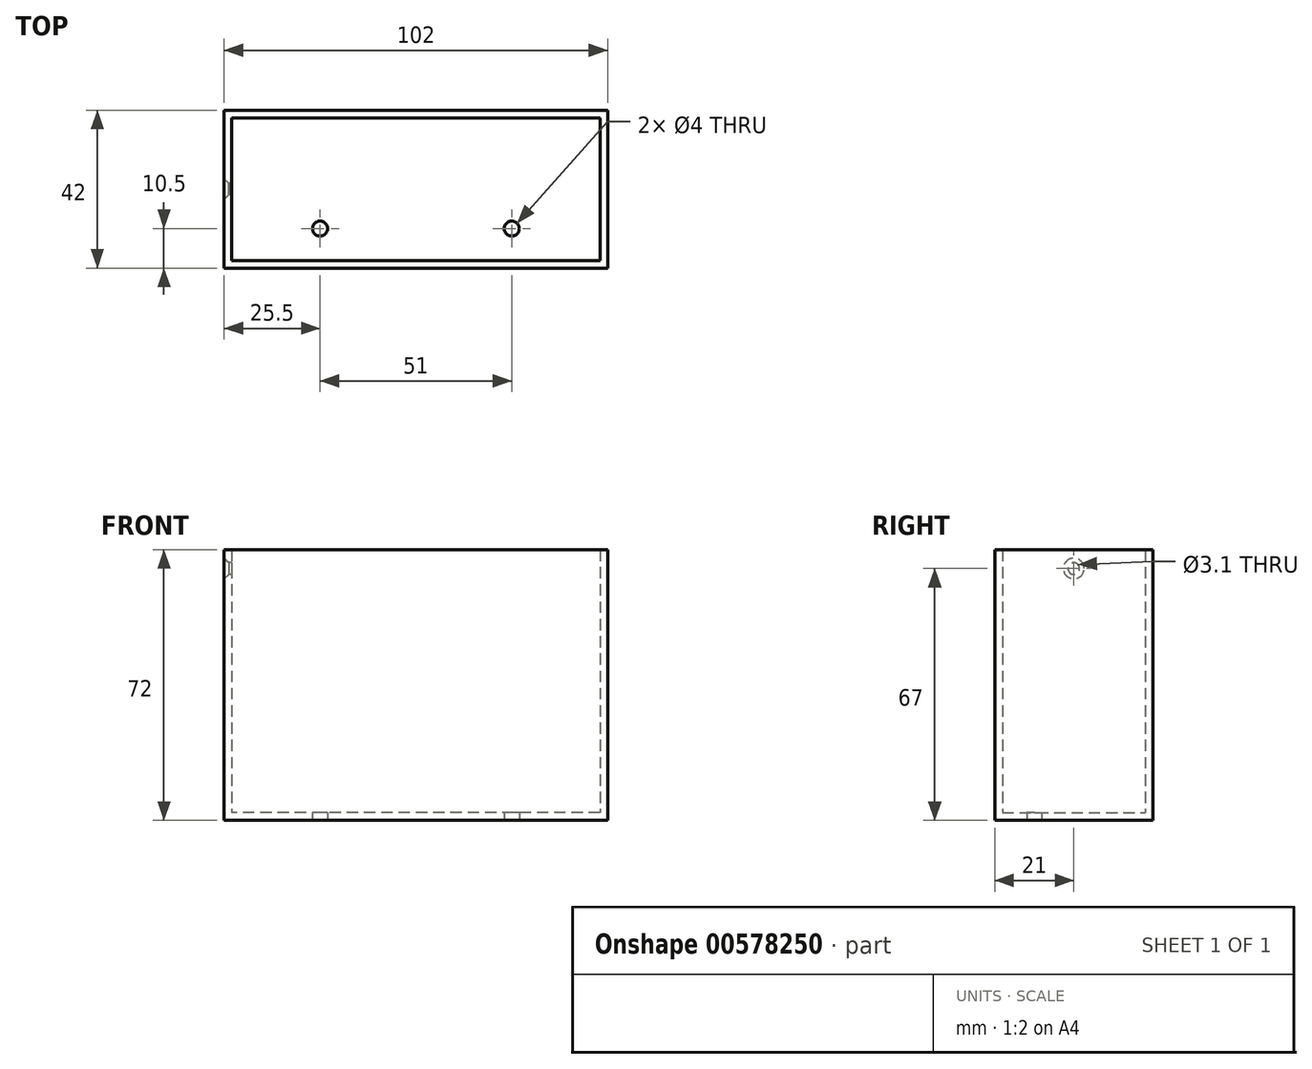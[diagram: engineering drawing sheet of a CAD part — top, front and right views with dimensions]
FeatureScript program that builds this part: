
annotation { "Feature Type Name" : "Feature", "Feature Type Description" : "" }
export const myFeature = defineFeature(function(context is Context, id is Id, definition is map)
    precondition{}
    {
        {
            assignVariable(context, id + "F0", {"name" : "wand", "anyValue" : 2});
        }
        {
            var Q0;
            Q0=qCreatedBy(makeId("Top.planeOp"),FACE);
            var sketch = newSketch(context, id + "F1", { "sketchPlane" : qUnion([Q0])});
            skLineSegment(sketch, "E0.bottom", {"start": v(51, -21) * mm, "end": v(-51, -21) * mm});
            skLineSegment(sketch, "E0.top", {"start": v(51, 21) * mm, "end": v(-51, 21) * mm});
            skLineSegment(sketch, "E0.left", {"start": v(51, -21) * mm, "end": v(51, 21) * mm});
            skLineSegment(sketch, "E0.right", {"start": v(-51, -21) * mm, "end": v(-51, 21) * mm});
            skPoint(sketch, "E0.middle", {"position": v(0, 0) * mm});
            skLineSegment(sketch, "E1.bottom", {"start": v(49, -19) * mm, "end": v(-49, -19) * mm});
            skLineSegment(sketch, "E1.top", {"start": v(49, 19) * mm, "end": v(-49, 19) * mm});
            skLineSegment(sketch, "E1.left", {"start": v(49, -19) * mm, "end": v(49, 19) * mm});
            skLineSegment(sketch, "E1.right", {"start": v(-49, -19) * mm, "end": v(-49, 19) * mm});
            skSolve(sketch);
        }
        {
            var Q0;
            Q0 = qSketchRegion(id + "F1", true);
            extrude(context, id + "F2", {"entities" : qUnion([Q0]), "depth" : 72 * mm, "offsetDistance" : 25 * mm});
        }
        {
            var Q0;
            Q0=makeQuery(id+"F2.opExtrude","CAP_FACE",FACE,{"disambiguationData":[OSD([sQuery(id+"F1.wireOp",EDGE,"E0.bottom"),sQuery(id+"F1.wireOp",EDGE,"E0.top"),sQuery(id+"F1.wireOp",EDGE,"E0.left"),sQuery(id+"F1.wireOp",EDGE,"E0.right")])],"isStart":true});
            var sketch = newSketch(context, id + "F3", { "sketchPlane" : qUnion([Q0])});
            skCircle(sketch, "E2", {"center": v(0, 0) * mm, "radius": 8.2 * mm});
            skSolve(sketch);
        }
        {
            var Q0;
            Q0=makeQuery(id+"F3.imprint","IMPRINT",FACE,{"disambiguationData":[TD([[makeQuery(id+"F3.imprint","IMPRINT",EDGE,{"derivedFrom":sQuery(id+"F3.wireOp",EDGE,"E2")}),1.0]])]});
            extrude(context, id + "F4", {"entities" : qUnion([Q0]), "operationType" : NewBodyOperationType.REMOVE, "oppositeDirection" : true, "depth" : 25 * mm, "offsetDistance" : 25 * mm});
        }
        {
            var Q0;
            Q0=makeQuery(id+"F2.opExtrude","SWEPT_FACE",FACE,{"disambiguationData":[OSD([sQuery(id+"F1.wireOp",EDGE,"E0.right")])]});
            var sketch = newSketch(context, id + "F5", { "sketchPlane" : qUnion([Q0])});
            skPoint(sketch, "E3", {"position": v(0, 67) * mm});
            skSolve(sketch);
        }
        {
            var Q0;
            Q0=sQuery(id+"F5.wireOp",VERTEX,"E3");
            var Q1;
            Q1=makeQuery(id+"F2.opExtrude","SWEPT_BODY",BODY,{"disambiguationData":[OSD([sQuery(id+"F1.wireOp",EDGE,"E0.bottom"),sQuery(id+"F1.wireOp",EDGE,"E0.top"),sQuery(id+"F1.wireOp",EDGE,"E0.left"),sQuery(id+"F1.wireOp",EDGE,"E0.right")])]});
            hole(context, id + "F6", {"style" : HoleStyle.C_SINK, "endStyle" : HoleEndStyle.BLIND, "holeDiameter" : 3.1 * mm, "cSinkDiameter" : 5.5 * mm, "cSinkAngle" : 90 * degree, "holeDepth" : 20 * mm, "isTappedThrough" : true, "tappedDepth" : 12 * mm, "tapClearance" : 3, "locations" : qUnion([Q0]), "scope" : qUnion([Q1])});
        }
        {
            var Q0;
            Q0=qCreatedBy(makeId("Top.planeOp"),FACE);
            var sketch = newSketch(context, id + "F7", { "sketchPlane" : qUnion([Q0])});
            skPoint(sketch, "E4.0", {"position": v(-51, -21) * mm});
            skLineSegment(sketch, "E5.bottom", {"start": v(-51, -21) * mm, "end": v(51, -21) * mm});
            skLineSegment(sketch, "E5.top", {"start": v(-51, 21) * mm, "end": v(51, 21) * mm});
            skLineSegment(sketch, "E5.left", {"start": v(-51, -21) * mm, "end": v(-51, 21) * mm});
            skLineSegment(sketch, "E5.right", {"start": v(51, -21) * mm, "end": v(51, 21) * mm});
            skPoint(sketch, "E5.middle", {"position": v(0, 0) * mm});
            skSolve(sketch);
        }
        {
            var Q0;
            Q0 = qSketchRegion(id + "F7", true);
            extrude(context, id + "F8", {"entities" : qUnion([Q0]), "operationType" : NewBodyOperationType.ADD, "depth" : (getVariable(context, 'wand')) * mm, "offsetDistance" : 25 * mm});
        }
        {
            var Q0;
            Q0=makeQuery(id+"F8.boolean.opBoolean","MERGE",FACE,{"derivedFrom":[makeQuery(id+"F2.opExtrude","CAP_FACE",FACE,{"disambiguationData":[OSD([sQuery(id+"F1.wireOp",EDGE,"E0.bottom"),sQuery(id+"F1.wireOp",EDGE,"E0.top"),sQuery(id+"F1.wireOp",EDGE,"E0.left"),sQuery(id+"F1.wireOp",EDGE,"E0.right"),sQuery(id+"F1.wireOp",EDGE,"E1.bottom"),sQuery(id+"F1.wireOp",EDGE,"E1.top"),sQuery(id+"F1.wireOp",EDGE,"E1.left"),sQuery(id+"F1.wireOp",EDGE,"E1.right")])],"isStart":true}),makeQuery(id+"F8.opExtrude","CAP_FACE",FACE,{"disambiguationData":[OSD([sQuery(id+"F7.wireOp",EDGE,"E5.bottom"),sQuery(id+"F7.wireOp",EDGE,"E5.top"),sQuery(id+"F7.wireOp",EDGE,"E5.left"),sQuery(id+"F7.wireOp",EDGE,"E5.right")])],"isStart":true})]});
            var sketch = newSketch(context, id + "F9", { "sketchPlane" : qUnion([Q0])});
            skLineSegment(sketch, "E6", {"start": v(51, 0) * mm, "end": v(0, 21) * mm, "construction": true});
            skLineSegment(sketch, "E7", {"start": v(0, 21) * mm, "end": v(-51, 0) * mm, "construction": true});
            skPoint(sketch, "E8", {"position": v(25.5, 10.5) * mm});
            skPoint(sketch, "E9", {"position": v(-25.5, 10.5) * mm});
            skSolve(sketch);
        }
        {
            var Q0;
            Q0=sQuery(id+"F9.wireOp",VERTEX,"E8");
            var Q1;
            Q1=sQuery(id+"F9.wireOp",VERTEX,"E9");
            var Q2;
            Q2=makeQuery(id+"F2.opExtrude","SWEPT_BODY",BODY,{"disambiguationData":[OSD([sQuery(id+"F1.wireOp",EDGE,"E0.bottom"),sQuery(id+"F1.wireOp",EDGE,"E0.top"),sQuery(id+"F1.wireOp",EDGE,"E0.left"),sQuery(id+"F1.wireOp",EDGE,"E0.right"),sQuery(id+"F1.wireOp",EDGE,"E1.bottom"),sQuery(id+"F1.wireOp",EDGE,"E1.top"),sQuery(id+"F1.wireOp",EDGE,"E1.left"),sQuery(id+"F1.wireOp",EDGE,"E1.right")])]});
            hole(context, id + "F10", {"style" : HoleStyle.SIMPLE, "endStyle" : HoleEndStyle.BLIND, "holeDiameter" : 4 * mm, "holeDepth" : 20 * mm, "isTappedThrough" : true, "tappedDepth" : 12 * mm, "tapClearance" : 3, "locations" : qUnion([Q0, Q1]), "scope" : qUnion([Q2])});
        }
    });
